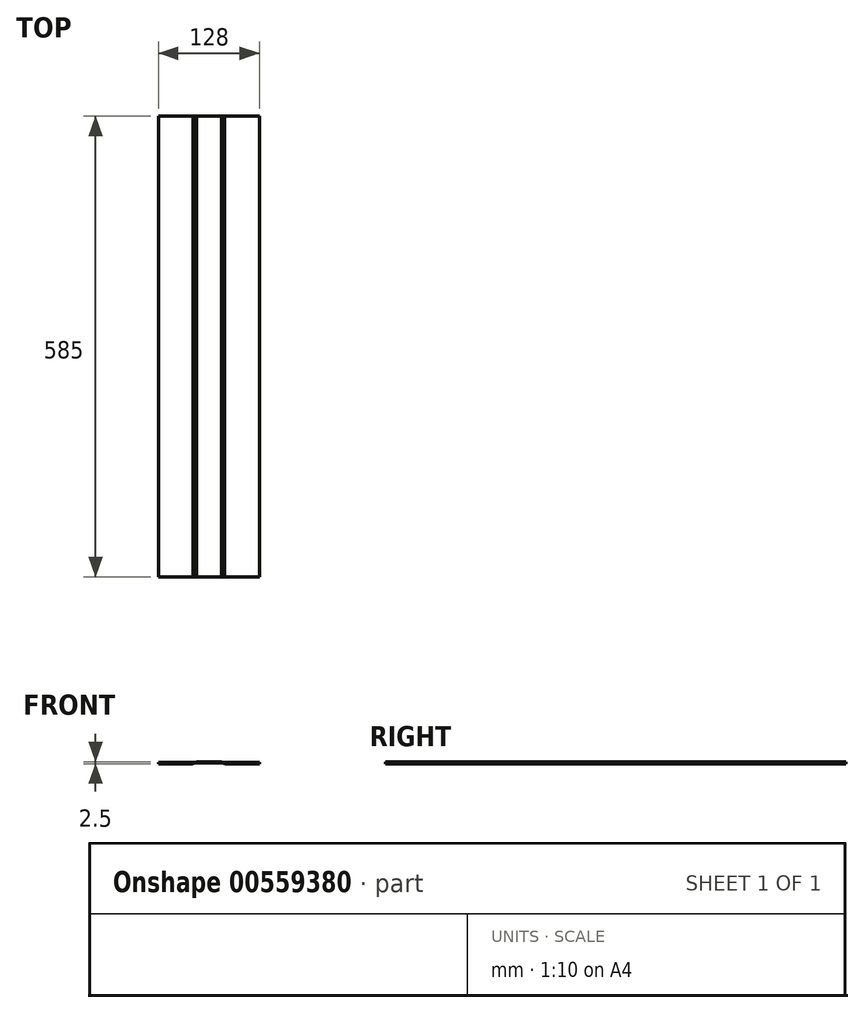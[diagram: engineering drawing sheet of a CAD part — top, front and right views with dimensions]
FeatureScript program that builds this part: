
annotation { "Feature Type Name" : "Feature", "Feature Type Description" : "" }
export const myFeature = defineFeature(function(context is Context, id is Id, definition is map)
    precondition{}
    {
        {
            var Q0;
            Q0=qCreatedBy(makeId("Front.planeOp"),FACE);
            var sketch = newSketch(context, id + "F0", { "sketchPlane" : qUnion([Q0])});
            skLineSegment(sketch, "E0", {"start": v(0, 0) * mm, "end": v(16, 0) * mm});
            skLineSegment(sketch, "E1", {"start": v(16, 0) * mm, "end": v(0, 0) * mm});
            skLineSegment(sketch, "E2", {"start": v(0, 0) * mm, "end": v(-16, 0) * mm});
            skLineSegment(sketch, "E3", {"start": v(20, -1) * mm, "end": v(64, -1) * mm});
            skLineSegment(sketch, "E4", {"start": v(-20, -1) * mm, "end": v(-64, -1) * mm});
            skLineSegment(sketch, "E5", {"start": v(-20, -1) * mm, "end": v(-16, 0) * mm});
            skLineSegment(sketch, "E6", {"start": v(20, -1) * mm, "end": v(16, 0) * mm});
            skLineSegment(sketch, "E7", {"start": v(64, -1) * mm, "end": v(64, 0.5) * mm});
            skLineSegment(sketch, "E8", {"start": v(20, 0.5) * mm, "end": v(64, 0.5) * mm});
            skLineSegment(sketch, "E9", {"start": v(16, 1.5) * mm, "end": v(20, 0.5) * mm});
            skLineSegment(sketch, "E10", {"start": v(0, 1.5) * mm, "end": v(16, 1.5) * mm});
            skLineSegment(sketch, "E11", {"start": v(0, 1.5) * mm, "end": v(-16, 1.5) * mm});
            skLineSegment(sketch, "E12", {"start": v(-20, 0.5) * mm, "end": v(-16, 1.5) * mm});
            skLineSegment(sketch, "E13", {"start": v(-64, -1) * mm, "end": v(-64, 0.5) * mm});
            skLineSegment(sketch, "E14", {"start": v(-64, 0.5) * mm, "end": v(-20, 0.5) * mm});
            skLineSegment(sketch, "E15", {"start": v(16, 1.5) * mm, "end": v(20, -1) * mm});
            skLineSegment(sketch, "E16", {"start": v(-16, 1.5) * mm, "end": v(-20, -1) * mm});
            skSolve(sketch);
        }
        {
            var Q0;
            Q0 = qSketchRegion(id + "F0", true);
            extrude(context, id + "F1", {"entities" : qUnion([Q0]), "depth" : 585 * mm, "offsetDistance" : 25 * mm});
        }
        {
            var Q0;
            Q0=makeQuery(id+"F1.opExtrude","SWEPT_EDGE",EDGE,{"disambiguationData":[OSD([sQuery(id+"F0.wireOp",EDGE,"E3"),sQuery(id+"F0.wireOp",EDGE,"E6"),sQuery(id+"F0.wireOp",EDGE,"E15")])]});
            var Q1;
            Q1=makeQuery(id+"F1.opExtrude","SWEPT_EDGE",EDGE,{"disambiguationData":[OSD([sQuery(id+"F0.wireOp",EDGE,"E1"),sQuery(id+"F0.wireOp",EDGE,"E6")])]});
            var Q2;
            Q2=makeQuery(id+"F1.opExtrude","SWEPT_EDGE",EDGE,{"disambiguationData":[OSD([sQuery(id+"F0.wireOp",EDGE,"E2"),sQuery(id+"F0.wireOp",EDGE,"E5")])]});
            var Q3;
            Q3=makeQuery(id+"F1.opExtrude","SWEPT_EDGE",EDGE,{"disambiguationData":[OSD([sQuery(id+"F0.wireOp",EDGE,"E4"),sQuery(id+"F0.wireOp",EDGE,"E5"),sQuery(id+"F0.wireOp",EDGE,"E16")])]});
            fillet(context, id + "F2", {"entities" : qUnion([Q0, Q1, Q2, Q3]), "radius" : 5 * mm, "tangentPropagation" : true, "allowEdgeOverflow" : false});
        }
    });
